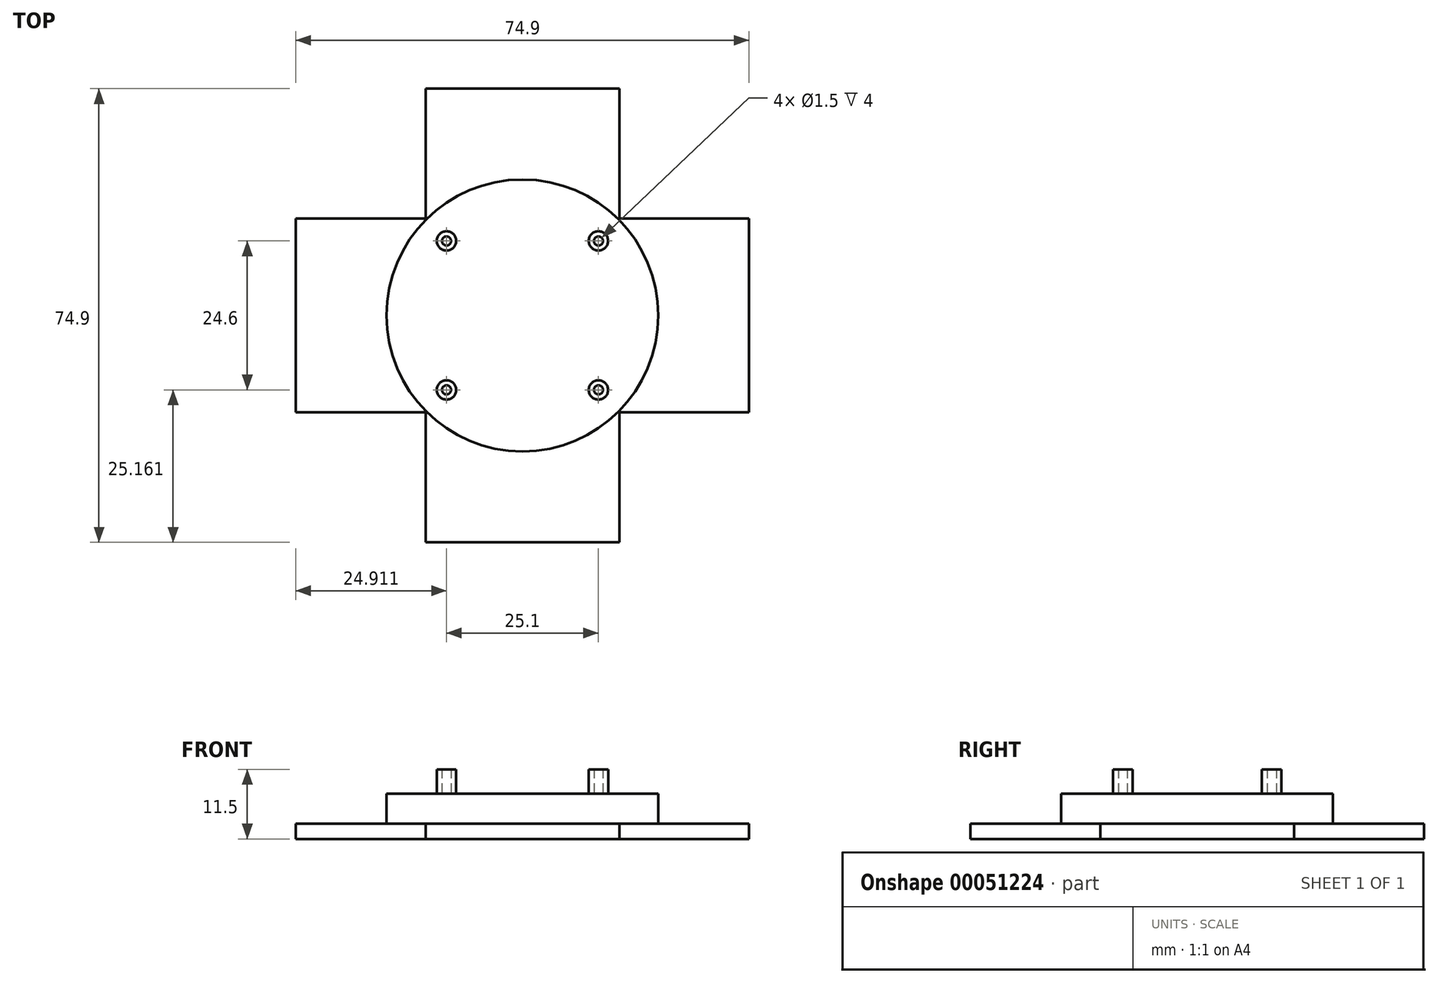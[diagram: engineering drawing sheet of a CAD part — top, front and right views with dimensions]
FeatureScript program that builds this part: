
annotation { "Feature Type Name" : "Feature", "Feature Type Description" : "" }
export const myFeature = defineFeature(function(context is Context, id is Id, definition is map)
    precondition{}
    {
        {
            var Q0;
            Q0=qCreatedBy(makeId("Top.planeOp"),FACE);
            var sketch = newSketch(context, id + "F0", { "sketchPlane" : qUnion([Q0])});
            skCircle(sketch, "E0", {"center": v(0, 0) * mm, "radius": 22.45 * mm});
            skSolve(sketch);
        }
        {
            var Q0;
            Q0=makeQuery(id+"F0.imprint","IMPRINT",FACE,{"disambiguationData":[TD([[makeQuery(id+"F0.imprint","IMPRINT",EDGE,{"derivedFrom":sQuery(id+"F0.wireOp",EDGE,"E0")}),1.0]])]});
            extrude(context, id + "F1", {"entities" : qUnion([Q0]), "depth" : 5 * mm});
        }
        {
            var Q0;
            Q0=qCreatedBy(makeId("Top.planeOp"),FACE);
            var sketch = newSketch(context, id + "F2", { "sketchPlane" : qUnion([Q0])});
            skLineSegment(sketch, "E1.bottom", {"start": v(-16, 37.45) * mm, "end": v(16, 37.45) * mm});
            skLineSegment(sketch, "E1.top", {"start": v(-16, -37.45) * mm, "end": v(16, -37.45) * mm});
            skLineSegment(sketch, "E1.left", {"start": v(-16, 37.45) * mm, "end": v(-16, -37.45) * mm});
            skLineSegment(sketch, "E1.right", {"start": v(16, 37.45) * mm, "end": v(16, -37.45) * mm});
            skLineSegment(sketch, "E2.bottom", {"start": v(-37.45, 16) * mm, "end": v(37.45, 16) * mm});
            skLineSegment(sketch, "E2.top", {"start": v(-37.45, -16) * mm, "end": v(37.45, -16) * mm});
            skLineSegment(sketch, "E2.left", {"start": v(-37.45, 16) * mm, "end": v(-37.45, -16) * mm});
            skLineSegment(sketch, "E2.right", {"start": v(37.45, 16) * mm, "end": v(37.45, -16) * mm});
            skSolve(sketch);
        }
        {
            var Q0;
            Q0 = qSketchRegion(id + "F2", true);
            extrude(context, id + "F3", {"entities" : qUnion([Q0]), "operationType" : NewBodyOperationType.ADD, "oppositeDirection" : true, "depth" : 2.5 * mm});
        }
        {
            var Q0;
            Q0=makeQuery(id+"F1.opExtrude","CAP_FACE",FACE,{"disambiguationData":[OSD([sQuery(id+"F0.wireOp",EDGE,"E0")])],"isStart":false});
            var sketch = newSketch(context, id + "F4", { "sketchPlane" : qUnion([Q0])});
            skCircle(sketch, "E3", {"center": v(12.56, -12.29) * mm, "radius": 1.6 * mm});
            skCircle(sketch, "E4", {"center": v(12.56, -12.29) * mm, "radius": 0.75 * mm});
            skCircle(sketch, "E5.0.1.0", {"center": v(12.56, 12.31) * mm, "radius": 0.75 * mm});
            skCircle(sketch, "E5.0.1.1", {"center": v(12.56, 12.31) * mm, "radius": 1.6 * mm});
            skCircle(sketch, "E5.1.0.0", {"center": v(-12.54, -12.29) * mm, "radius": 0.75 * mm});
            skCircle(sketch, "E5.1.0.1", {"center": v(-12.54, -12.29) * mm, "radius": 1.6 * mm});
            skCircle(sketch, "E5.1.1.0", {"center": v(-12.54, 12.31) * mm, "radius": 0.75 * mm});
            skCircle(sketch, "E5.1.1.1", {"center": v(-12.54, 12.31) * mm, "radius": 1.6 * mm});
            skLineSegment(sketch, "E5.direction1", {"start": v(12.56, -12.29) * mm, "end": v(-12.54, -12.29) * mm, "construction": true});
            skLineSegment(sketch, "E5.direction2", {"start": v(12.56, -12.29) * mm, "end": v(12.56, 12.31) * mm, "construction": true});
            skSolve(sketch);
        }
        {
            var Q0;
            Q0=makeQuery(id+"F4.imprint","IMPRINT",FACE,{"disambiguationData":[TD([[makeQuery(id+"F4.imprint","IMPRINT",EDGE,{"derivedFrom":sQuery(id+"F4.wireOp",EDGE,"E5.0.1.0")}),-1.0]])]});
            var Q1;
            Q1=makeQuery(id+"F4.imprint","IMPRINT",FACE,{"disambiguationData":[TD([[makeQuery(id+"F4.imprint","IMPRINT",EDGE,{"derivedFrom":sQuery(id+"F4.wireOp",EDGE,"E5.1.1.0")}),-1.0]])]});
            var Q2;
            Q2=makeQuery(id+"F4.imprint","IMPRINT",FACE,{"disambiguationData":[TD([[makeQuery(id+"F4.imprint","IMPRINT",EDGE,{"derivedFrom":sQuery(id+"F4.wireOp",EDGE,"E5.1.0.0")}),-1.0]])]});
            var Q3;
            Q3=makeQuery(id+"F4.imprint","IMPRINT",FACE,{"disambiguationData":[TD([[makeQuery(id+"F4.imprint","IMPRINT",EDGE,{"derivedFrom":sQuery(id+"F4.wireOp",EDGE,"E3")}),1.0]])]});
            extrude(context, id + "F5", {"entities" : qUnion([Q0, Q1, Q2, Q3]), "operationType" : NewBodyOperationType.ADD, "depth" : 4 * mm});
        }
    });
